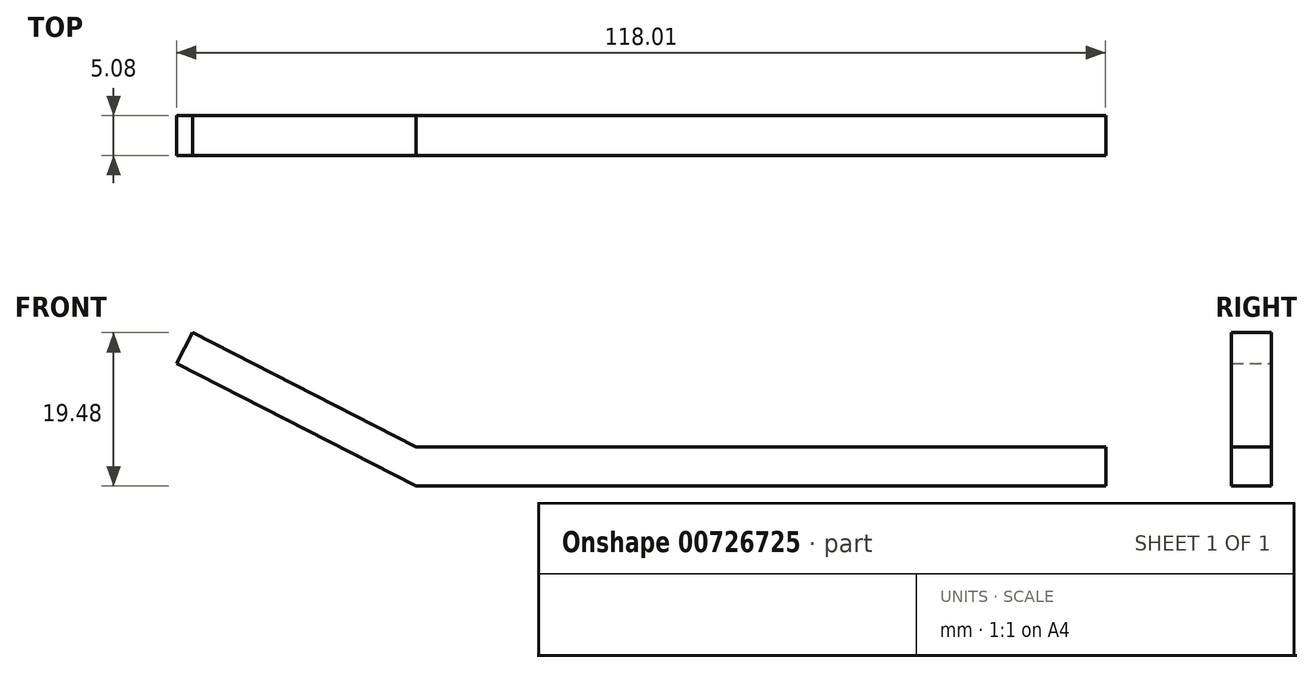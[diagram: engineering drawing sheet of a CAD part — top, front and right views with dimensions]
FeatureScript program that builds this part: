
annotation { "Feature Type Name" : "Feature", "Feature Type Description" : "" }
export const myFeature = defineFeature(function(context is Context, id is Id, definition is map)
    precondition{}
    {
        {
            var Q0;
            Q0=qCreatedBy(makeId("Front.planeOp"),FACE);
            var sketch = newSketch(context, id + "F0", { "sketchPlane" : qUnion([Q0])});
            skLineSegment(sketch, "E0", {"start": v(46.4, -5.24) * mm, "end": v(-41.37, -5.24) * mm});
            skLineSegment(sketch, "E1", {"start": v(-41.37, -5.24) * mm, "end": v(-79.36, 16.37) * mm});
            skLineSegment(sketch, "E2", {"start": v(-79.36, 16.37) * mm, "end": v(-81.83, 12.02) * mm});
            skLineSegment(sketch, "E3", {"start": v(-81.83, 12.02) * mm, "end": v(-41.37, -8.73) * mm});
            skLineSegment(sketch, "E4", {"start": v(-41.37, -8.73) * mm, "end": v(47.7, -8.73) * mm});
            skLineSegment(sketch, "E5", {"start": v(47.7, -8.73) * mm, "end": v(46.4, -5.24) * mm});
            skSolve(sketch);
        }
        {
            var Q0;
            Q0 = qSketchRegion(id + "F0", true);
            extrude(context, id + "F1", {"entities" : qUnion([Q0]), "depth" : 5.08 * mm, "offsetDistance" : 25.4 * mm});
        }
        {
            var Q0;
            Q0=makeQuery(id+"F1.opExtrude","SWEPT_BODY",BODY,{"disambiguationData":[OSD([sQuery(id+"F0.wireOp",EDGE,"E0"),sQuery(id+"F0.wireOp",EDGE,"E1"),sQuery(id+"F0.wireOp",EDGE,"E2"),sQuery(id+"F0.wireOp",EDGE,"E3"),sQuery(id+"F0.wireOp",EDGE,"E4"),sQuery(id+"F0.wireOp",EDGE,"E5")])]});
            deleteBodies(context, id + "F2", {"entities" : qUnion([Q0])});
        }
        {
            var Q0;
            Q0=qCreatedBy(makeId("Front.planeOp"),FACE);
            var sketch = newSketch(context, id + "F3", { "sketchPlane" : qUnion([Q0])});
            skLineSegment(sketch, "E6", {"start": v(44.68, 6.68) * mm, "end": v(-42.91, 6.68) * mm});
            skLineSegment(sketch, "E7", {"start": v(-42.91, 6.68) * mm, "end": v(-71.32, 21.23) * mm});
            skLineSegment(sketch, "E8", {"start": v(-71.32, 21.23) * mm, "end": v(-73.33, 17.32) * mm});
            skLineSegment(sketch, "E9", {"start": v(-73.33, 17.32) * mm, "end": v(-42.91, 1.75) * mm});
            skLineSegment(sketch, "E10", {"start": v(-42.91, 1.75) * mm, "end": v(44.68, 1.75) * mm});
            skLineSegment(sketch, "E11", {"start": v(44.68, 1.75) * mm, "end": v(44.68, 6.68) * mm});
            skSolve(sketch);
        }
        {
            var Q0;
            Q0 = qSketchRegion(id + "F3", true);
            extrude(context, id + "F4", {"entities" : qUnion([Q0]), "depth" : 5.08 * mm, "offsetDistance" : 25.4 * mm});
        }
    });
